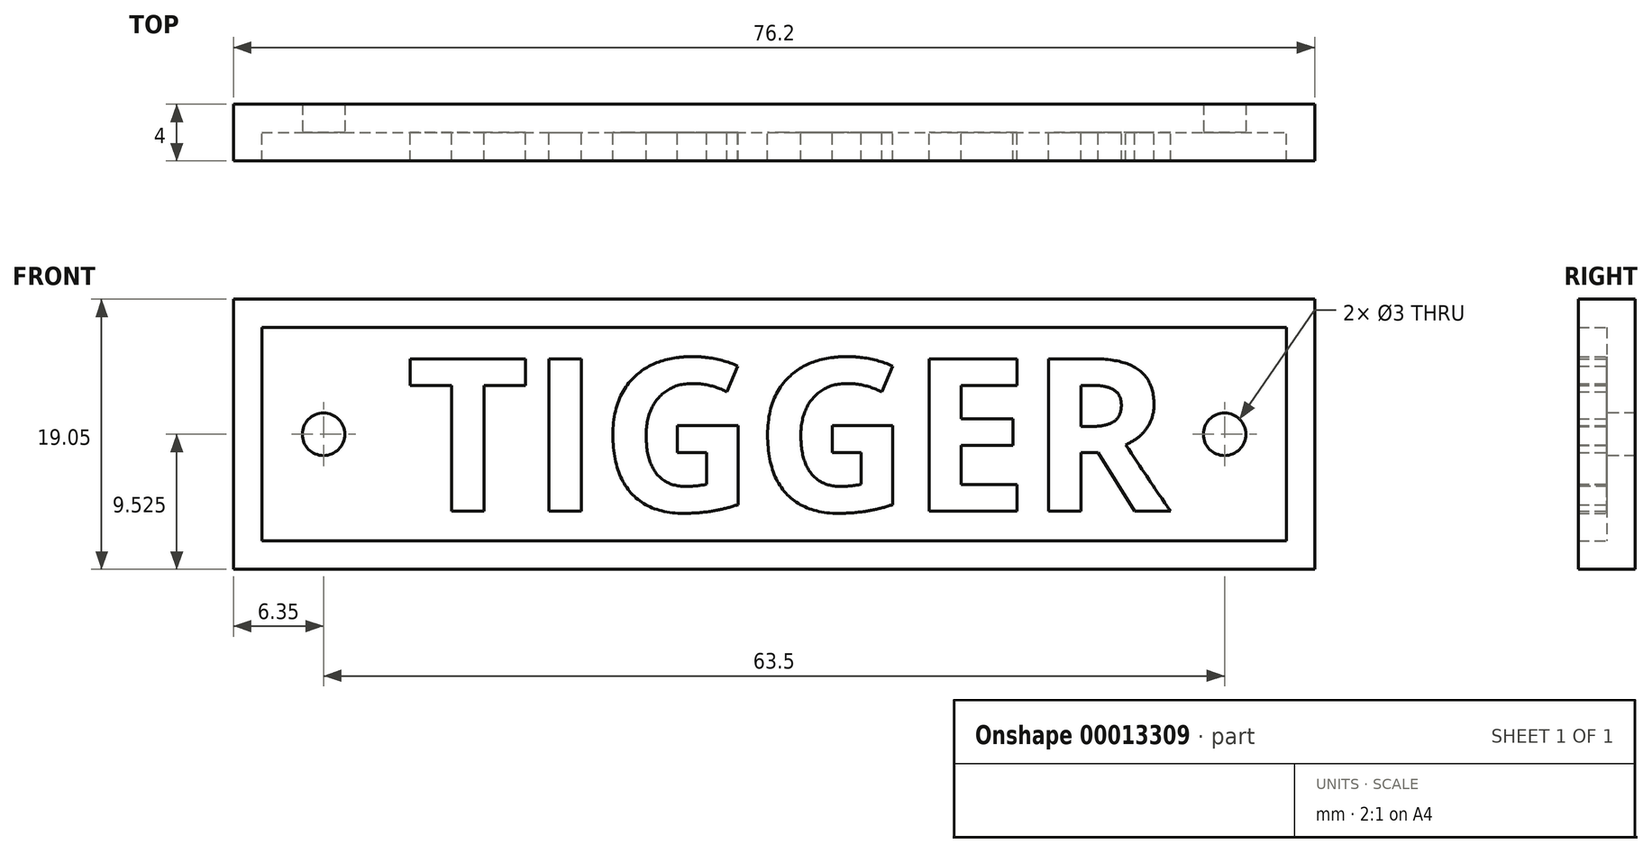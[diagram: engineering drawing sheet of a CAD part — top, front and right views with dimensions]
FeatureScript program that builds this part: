
annotation { "Feature Type Name" : "Feature", "Feature Type Description" : "" }
export const myFeature = defineFeature(function(context is Context, id is Id, definition is map)
    precondition{}
    {
        {
            var Q0;
            Q0=qCreatedBy(makeId("Front.planeOp"),FACE);
            var sketch = newSketch(context, id + "F0", { "sketchPlane" : qUnion([Q0])});
            skLineSegment(sketch, "E0.bottom", {"start": v(76.2, 19.05) * mm, "end": v(0, 19.05) * mm});
            skLineSegment(sketch, "E0.top", {"start": v(76.2, 0) * mm, "end": v(0, 0) * mm});
            skLineSegment(sketch, "E0.left", {"start": v(76.2, 19.05) * mm, "end": v(76.2, 0) * mm});
            skLineSegment(sketch, "E0.right", {"start": v(0, 19.05) * mm, "end": v(0, 0) * mm});
            skSolve(sketch);
        }
        {
            var Q0;
            Q0 = qSketchRegion(id + "F0", true);
            extrude(context, id + "F1", {"entities" : qUnion([Q0]), "depth" : 2 * mm});
        }
        {
            var Q0;
            Q0=makeQuery(id+"F1.opExtrude","CAP_FACE",FACE,{"disambiguationData":[OSD([sQuery(id+"F0.wireOp",EDGE,"E0.bottom"),sQuery(id+"F0.wireOp",EDGE,"E0.top"),sQuery(id+"F0.wireOp",EDGE,"E0.left"),sQuery(id+"F0.wireOp",EDGE,"E0.right")])],"isStart":false});
            var sketch = newSketch(context, id + "F2", { "sketchPlane" : qUnion([Q0])});
            skLineSegment(sketch, "E1.bottom", {"start": v(0, 0) * mm, "end": v(76.2, 0) * mm});
            skLineSegment(sketch, "E1.top", {"start": v(0, 19.05) * mm, "end": v(76.2, 19.05) * mm});
            skLineSegment(sketch, "E1.left", {"start": v(0, 0) * mm, "end": v(0, 19.05) * mm});
            skLineSegment(sketch, "E1.right", {"start": v(76.2, 0) * mm, "end": v(76.2, 19.05) * mm});
            skLineSegment(sketch, "E2.bottom", {"start": v(2, 17.05) * mm, "end": v(74.2, 17.05) * mm});
            skLineSegment(sketch, "E2.top", {"start": v(2, 2) * mm, "end": v(74.2, 2) * mm});
            skLineSegment(sketch, "E2.left", {"start": v(2, 17.05) * mm, "end": v(2, 2) * mm});
            skLineSegment(sketch, "E2.right", {"start": v(74.2, 17.05) * mm, "end": v(74.2, 2) * mm});
            skSolve(sketch);
        }
        {
            var Q0;
            Q0 = qSketchRegion(id + "F2", true);
            extrude(context, id + "F3", {"entities" : qUnion([Q0]), "operationType" : NewBodyOperationType.ADD, "depth" : 2 * mm});
        }
        {
            var Q0;
            Q0=makeQuery(id+"F1.opExtrude","CAP_FACE",FACE,{"disambiguationData":[OSD([sQuery(id+"F0.wireOp",EDGE,"E0.bottom"),sQuery(id+"F0.wireOp",EDGE,"E0.top"),sQuery(id+"F0.wireOp",EDGE,"E0.left"),sQuery(id+"F0.wireOp",EDGE,"E0.right")])],"isStart":false});
            var sketch = newSketch(context, id + "F4", { "sketchPlane" : qUnion([Q0])});
            skLineSegment(sketch, "E3.bottom", {"start": v(12.16, 14.95) * mm, "end": v(66.03, 14.95) * mm});
            skLineSegment(sketch, "E3.left", {"start": v(12.16, 14.95) * mm, "end": v(12.16, 4.1) * mm});
            skText(sketch, "E4", { "text": "TIGGER", "fontName": "OpenSans-Bold.ttf"});
            const initialGuessF4  = {"E4": [0.01216, 0.0041, 1, 0, 0.01084]};
            skSetInitialGuess(sketch, initialGuessF4);
            skSolve(sketch);
        }
        {
            var Q0;
            Q0 = qSketchRegion(id + "F4", true);
            extrude(context, id + "F5", {"entities" : qUnion([Q0]), "operationType" : NewBodyOperationType.ADD, "depth" : 2 * mm});
        }
        {
            var Q0;
            Q0=makeQuery(id+"F5.boolean.opBoolean","SPLIT",FACE,{"disambiguationData":[TD([makeQuery(id+"F3.opExtrude","SWEPT_FACE",FACE,{"disambiguationData":[OSD([sQuery(id+"F2.wireOp",EDGE,"E2.bottom")])]})])],"derivedFrom":makeQuery(id+"F1.opExtrude","CAP_FACE",FACE,{"disambiguationData":[OSD([sQuery(id+"F0.wireOp",EDGE,"E0.bottom"),sQuery(id+"F0.wireOp",EDGE,"E0.top"),sQuery(id+"F0.wireOp",EDGE,"E0.left"),sQuery(id+"F0.wireOp",EDGE,"E0.right")])],"isStart":false})});
            var sketch = newSketch(context, id + "F6", { "sketchPlane" : qUnion([Q0])});
            skCircle(sketch, "E5", {"center": v(6.35, 9.53) * mm, "radius": 1.5 * mm});
            skPoint(sketch, "E5.centerSnap0", {"position": v(2, 9.53) * mm});
            skCircle(sketch, "E6", {"center": v(69.85, 9.53) * mm, "radius": 1.5 * mm});
            skSolve(sketch);
        }
        {
            var Q0;
            Q0 = qSketchRegion(id + "F6", true);
            extrude(context, id + "F7", {"entities" : qUnion([Q0]), "operationType" : NewBodyOperationType.REMOVE, "endBound" : BoundingType.THROUGH_ALL, "oppositeDirection" : true, "depth" : 25.4 * mm});
        }
    });
